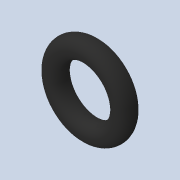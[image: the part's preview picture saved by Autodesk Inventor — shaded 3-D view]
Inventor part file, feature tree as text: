
AUTODESK INVENTOR PART (.ipt)
format: ipt  version: 2020.4 (Build 244396000, 396)  size: 142,848 bytes
history: native  units: mm
features: sketch x2, sweep x1
ambient origin geometry x8: Origin, YZ Plane, XZ Plane, XY Plane, X Axis, Y Axis, Z Axis, Center Point
bodies: Solid1 (feature_tree)
feature tree (3):
  sweep  "Tire Base"
  sketch  "Sketch1"  dims[d0=5.255mm d1=2.1mm]
  sketch  "Sketch2"  dims[d2=3.6mm d3=0.0mm d4=0.0mm]
